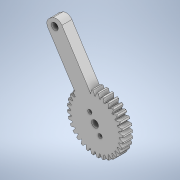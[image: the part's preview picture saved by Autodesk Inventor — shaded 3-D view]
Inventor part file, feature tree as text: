
AUTODESK INVENTOR PART (.ipt)
format: ipt  version: 2022 (Build 260153000, 153)  size: 1,047,552 bytes
history: native  units: in
note: dims shown in document units (in); Inventor stores cm internally (conversion verified against a paired STEP export)
features: sketch x6, extrude x5, projected_geometry x3, fillet x1, pattern_circular x1
ambient origin geometry x8: Origin, YZ Plane, XZ Plane, XY Plane, X Axis, Y Axis, Z Axis, Center Point
bodies: Solid1 (feature_tree)
feature tree (16):
  sketch  "Sketch1"  dims[d0=1.0in d1=1.0in d2=0.0in]
  extrude  "Extrusion1"  Depth=1.0in TaperAngle=0.0deg
  extrude  "Extrusion13"  Depth=0.13in
  extrude  "Extrusion14"  Depth=1.0in
  fillet  "Fillet1"  Radius=1.0in
  extrude  "Extrusion15"  Depth=0.125in
  extrude  "Extrusion16"  Depth=0.0787in
  sketch  "Sketch2"  dims[d3=0.8in d37=0.13in]
  sketch  "Sketch14"  dims[d38=1.0in d39=0.0in d40=1.55in d41=1.0in d42=0.0in]
  projected_geometry  "Projected Loop3"
  sketch  "Sketch15"  dims[d43=0.125in d44=0.1772in]
  projected_geometry  "Projected Loop4"
  sketch  "Sketch16"  dims[d45=0.3543in d46=0.0787in]
  sketch  "Sketch17"  dims[d47=0.0787in d48=1.0in d49=0.0in d50=0.13in d51=1.0in d52=0.0in]
  projected_geometry  "Projected Loop5"
  pattern_circular  "CirPattern1"
